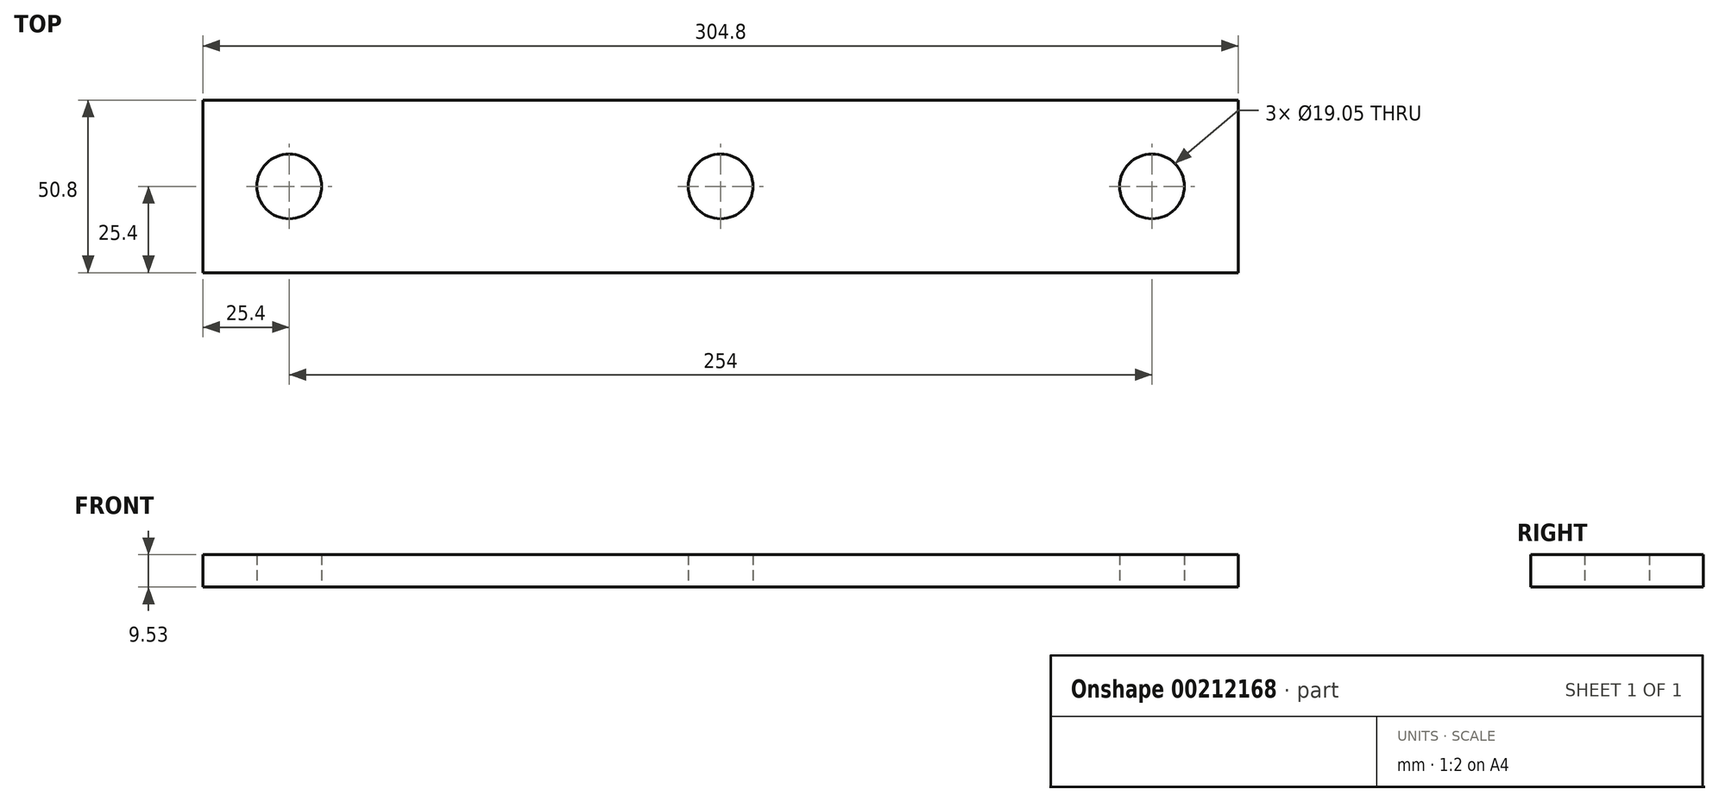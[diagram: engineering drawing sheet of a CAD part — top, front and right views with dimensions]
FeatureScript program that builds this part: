
annotation { "Feature Type Name" : "Feature", "Feature Type Description" : "" }
export const myFeature = defineFeature(function(context is Context, id is Id, definition is map)
    precondition{}
    {
        {
            var Q0;
            Q0=qCreatedBy(makeId("Top.planeOp"),FACE);
            var sketch = newSketch(context, id + "F0", { "sketchPlane" : qUnion([Q0])});
            skLineSegment(sketch, "E0.bottom", {"start": v(152.4, -25.4) * mm, "end": v(-152.4, -25.4) * mm});
            skLineSegment(sketch, "E0.top", {"start": v(152.4, 25.4) * mm, "end": v(-152.4, 25.4) * mm});
            skLineSegment(sketch, "E0.left", {"start": v(152.4, -25.4) * mm, "end": v(152.4, 25.4) * mm});
            skLineSegment(sketch, "E0.right", {"start": v(-152.4, -25.4) * mm, "end": v(-152.4, 25.4) * mm});
            skPoint(sketch, "E0.middle", {"position": v(0, 0) * mm});
            skPoint(sketch, "E1", {"position": v(-127, 0) * mm});
            skPoint(sketch, "E2", {"position": v(127, 0) * mm});
            skCircle(sketch, "E3", {"center": v(-127, 0) * mm, "radius": 9.53 * mm});
            skCircle(sketch, "E4", {"center": v(0, 0) * mm, "radius": 9.53 * mm});
            skCircle(sketch, "E5", {"center": v(127, 0) * mm, "radius": 9.53 * mm});
            skSolve(sketch);
        }
        {
            var Q0;
            Q0=makeQuery(id+"F0.imprint","IMPRINT",FACE,{"disambiguationData":[TD([[makeQuery(id+"F0.imprint","IMPRINT",EDGE,{"derivedFrom":sQuery(id+"F0.wireOp",EDGE,"E0.bottom")}),-1.0]])]});
            extrude(context, id + "F1", {"entities" : qUnion([Q0]), "depth" : 9.52 * mm});
        }
    });
